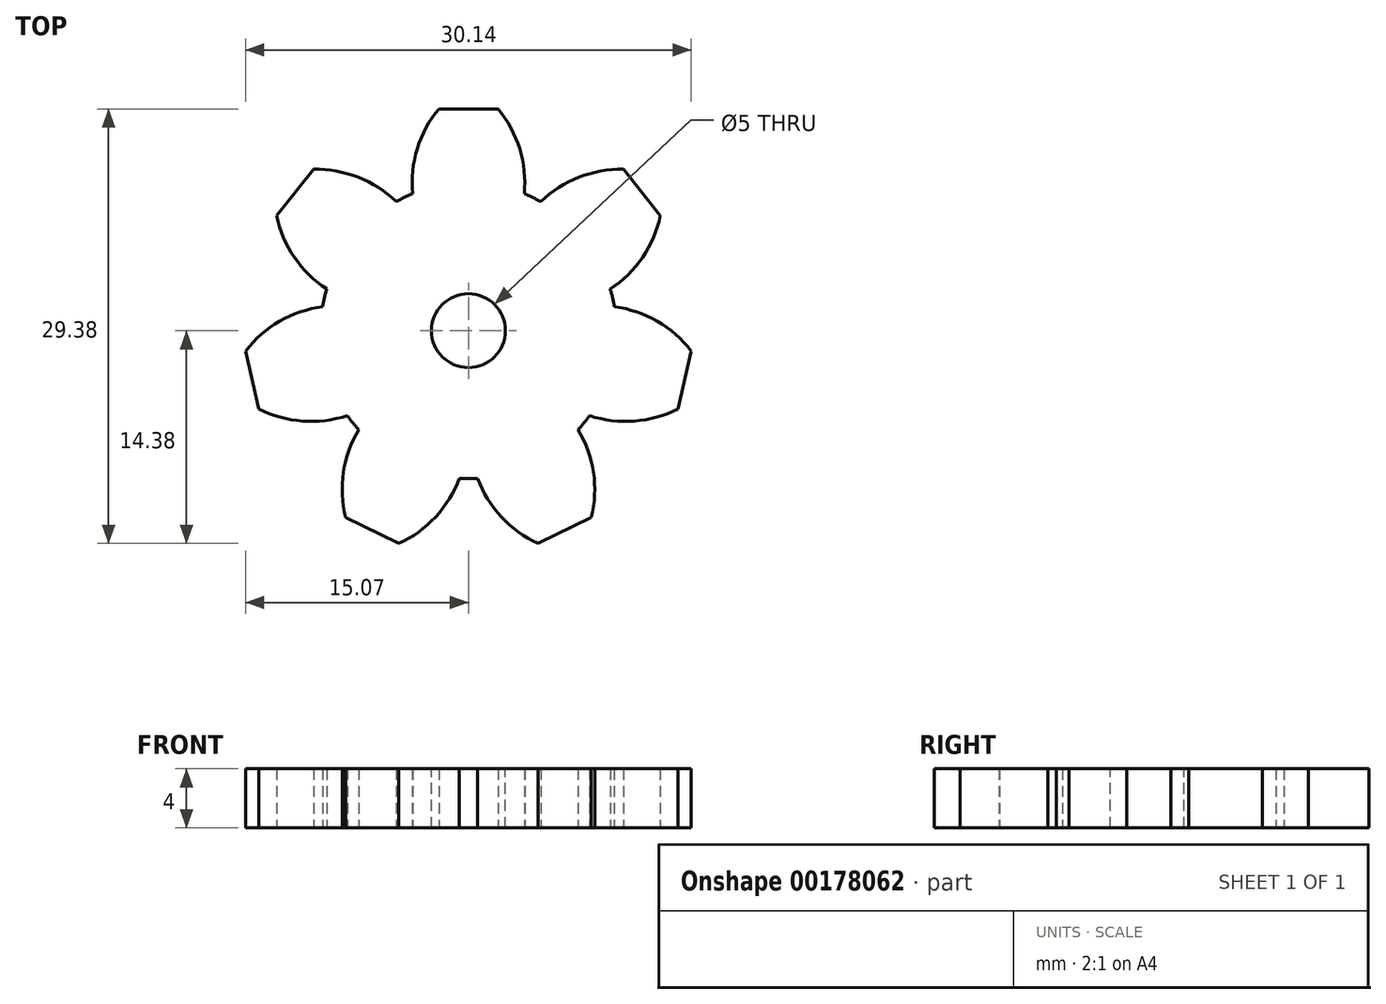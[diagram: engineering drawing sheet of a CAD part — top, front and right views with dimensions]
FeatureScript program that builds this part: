
annotation { "Feature Type Name" : "Feature", "Feature Type Description" : "" }
export const myFeature = defineFeature(function(context is Context, id is Id, definition is map)
    precondition{}
    {
        {
            var Q0;
            Q0=qCreatedBy(makeId("Top.planeOp"),FACE);
            var sketch = newSketch(context, id + "F0", { "sketchPlane" : qUnion([Q0])});
            skCircle(sketch, "E0", {"center": v(0, 0) * mm, "radius": 10 * mm});
            skLineSegment(sketch, "E1", {"start": v(0, 0) * mm, "end": v(0, 10) * mm, "construction": true});
            skLineSegment(sketch, "E2", {"start": v(0, 15) * mm, "end": v(-2, 15) * mm});
            skArc(sketch, "E3", {"start": v(-2, 15) * mm, "mid": v(-3.46, 12.3) * mm, "end": v(-3.78, 9.26) * mm});
            skLineSegment(sketch, "E4.MirrorCS", {"start": v(0, 15) * mm, "end": v(2, 15) * mm});
            skArc(sketch, "E5.MirrorCS", {"start": v(2, 15) * mm, "mid": v(3.46, 12.3) * mm, "end": v(3.78, 9.26) * mm});
            skArc(sketch, "E6.1.0", {"start": v(-12.97, 7.79) * mm, "mid": v(-11.78, 4.97) * mm, "end": v(-9.6, 2.82) * mm});
            skLineSegment(sketch, "E6.1.1", {"start": v(-11.73, 9.35) * mm, "end": v(-12.97, 7.79) * mm});
            skLineSegment(sketch, "E6.1.2", {"start": v(-11.73, 9.35) * mm, "end": v(-10.48, 10.92) * mm});
            skArc(sketch, "E6.1.3", {"start": v(-10.48, 10.92) * mm, "mid": v(-7.46, 10.38) * mm, "end": v(-4.89, 8.73) * mm});
            skArc(sketch, "E6.2.0", {"start": v(-14.18, -5.29) * mm, "mid": v(-11.23, -6.11) * mm, "end": v(-8.19, -5.74) * mm});
            skLineSegment(sketch, "E6.2.1", {"start": v(-14.62, -3.34) * mm, "end": v(-14.18, -5.29) * mm});
            skLineSegment(sketch, "E6.2.2", {"start": v(-14.62, -3.34) * mm, "end": v(-15.07, -1.39) * mm});
            skArc(sketch, "E6.2.3", {"start": v(-15.07, -1.39) * mm, "mid": v(-12.77, 0.64) * mm, "end": v(-9.87, 1.62) * mm});
            skArc(sketch, "E6.3.0", {"start": v(-4.7, -14.38) * mm, "mid": v(-2.22, -12.6) * mm, "end": v(-0.62, -9.98) * mm});
            skLineSegment(sketch, "E6.3.1", {"start": v(-6.5, -13.51) * mm, "end": v(-4.7, -14.38) * mm});
            skLineSegment(sketch, "E6.3.2", {"start": v(-6.5, -13.51) * mm, "end": v(-8.31, -12.65) * mm});
            skArc(sketch, "E6.3.3", {"start": v(-8.31, -12.65) * mm, "mid": v(-8.46, -9.59) * mm, "end": v(-7.42, -6.7) * mm});
            skArc(sketch, "E6.4.0", {"start": v(8.31, -12.65) * mm, "mid": v(8.46, -9.59) * mm, "end": v(7.42, -6.7) * mm});
            skLineSegment(sketch, "E6.4.1", {"start": v(6.5, -13.51) * mm, "end": v(8.31, -12.65) * mm});
            skLineSegment(sketch, "E6.4.2", {"start": v(6.5, -13.51) * mm, "end": v(4.7, -14.38) * mm});
            skArc(sketch, "E6.4.3", {"start": v(4.7, -14.38) * mm, "mid": v(2.22, -12.6) * mm, "end": v(0.62, -9.98) * mm});
            skArc(sketch, "E6.5.0", {"start": v(15.07, -1.39) * mm, "mid": v(12.77, 0.64) * mm, "end": v(9.87, 1.62) * mm});
            skLineSegment(sketch, "E6.5.1", {"start": v(14.62, -3.34) * mm, "end": v(15.07, -1.39) * mm});
            skLineSegment(sketch, "E6.5.2", {"start": v(14.62, -3.34) * mm, "end": v(14.18, -5.29) * mm});
            skArc(sketch, "E6.5.3", {"start": v(14.18, -5.29) * mm, "mid": v(11.23, -6.11) * mm, "end": v(8.19, -5.74) * mm});
            skArc(sketch, "E7.3.6.0", {"start": v(10.48, 10.92) * mm, "mid": v(7.46, 10.38) * mm, "end": v(4.89, 8.73) * mm});
            skLineSegment(sketch, "E7.4.6.0", {"start": v(11.73, 9.35) * mm, "end": v(10.48, 10.92) * mm});
            skLineSegment(sketch, "E7.7.6.0", {"start": v(11.73, 9.35) * mm, "end": v(12.97, 7.79) * mm});
            skArc(sketch, "E7.10.6.0", {"start": v(12.97, 7.79) * mm, "mid": v(11.78, 4.97) * mm, "end": v(9.6, 2.82) * mm});
            skSolve(sketch);
        }
        {
            var Q0;
            Q0=qSketchRegion(id+"F0",true);
            extrude(context, id + "F1", {"entities" : qUnion([Q0]), "depth" : 4 * mm});
        }
        {
            var Q0;
            Q0=makeQuery(id+"F1.opExtrude","CAP_FACE",FACE,{"disambiguationData":[OSD([sQuery(id+"F0.wireOp",EDGE,"E0"),sQuery(id+"F0.wireOp",EDGE,"E2"),sQuery(id+"F0.wireOp",EDGE,"E3"),sQuery(id+"F0.wireOp",EDGE,"E4.MirrorCS"),sQuery(id+"F0.wireOp",EDGE,"E5.MirrorCS"),sQuery(id+"F0.wireOp",EDGE,"E6.1.0"),sQuery(id+"F0.wireOp",EDGE,"E6.1.1"),sQuery(id+"F0.wireOp",EDGE,"E6.1.2"),sQuery(id+"F0.wireOp",EDGE,"E6.1.3"),sQuery(id+"F0.wireOp",EDGE,"E6.2.0"),sQuery(id+"F0.wireOp",EDGE,"E6.2.1"),sQuery(id+"F0.wireOp",EDGE,"E6.2.2"),sQuery(id+"F0.wireOp",EDGE,"E6.2.3"),sQuery(id+"F0.wireOp",EDGE,"E6.3.0"),sQuery(id+"F0.wireOp",EDGE,"E6.3.1"),sQuery(id+"F0.wireOp",EDGE,"E6.3.2"),sQuery(id+"F0.wireOp",EDGE,"E6.3.3"),sQuery(id+"F0.wireOp",EDGE,"E6.4.0"),sQuery(id+"F0.wireOp",EDGE,"E6.4.1"),sQuery(id+"F0.wireOp",EDGE,"E6.4.2"),sQuery(id+"F0.wireOp",EDGE,"E6.4.3"),sQuery(id+"F0.wireOp",EDGE,"E6.5.0"),sQuery(id+"F0.wireOp",EDGE,"E6.5.1"),sQuery(id+"F0.wireOp",EDGE,"E6.5.2"),sQuery(id+"F0.wireOp",EDGE,"E6.5.3"),sQuery(id+"F0.wireOp",EDGE,"E6.6.0"),sQuery(id+"F0.wireOp",EDGE,"E6.6.1"),sQuery(id+"F0.wireOp",EDGE,"E6.6.2"),sQuery(id+"F0.wireOp",EDGE,"E6.6.3")])],"isStart":false});
            var sketch = newSketch(context, id + "F2", { "sketchPlane" : qUnion([Q0])});
            skCircle(sketch, "E8", {"center": v(0, 0) * mm, "radius": 2.5 * mm});
            skSolve(sketch);
        }
        {
            var Q0;
            Q0=qSketchRegion(id+"F2",true);
            extrude(context, id + "F3", {"entities" : qUnion([Q0]), "operationType" : NewBodyOperationType.REMOVE, "endBound" : BoundingType.THROUGH_ALL, "oppositeDirection" : true, "depth" : 25 * mm});
        }
    });
